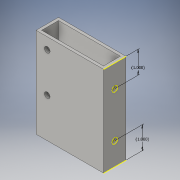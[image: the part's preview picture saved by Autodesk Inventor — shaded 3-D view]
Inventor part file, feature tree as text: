
AUTODESK INVENTOR PART (.ipt)
format: ipt  version: 2016 (Build 200138000, 138)  size: 123,904 bytes
history: native  units: in
note: dims shown in document units (in); Inventor stores cm internally (conversion verified against a paired STEP export)
features: sketch x4, extrude x3
ambient origin geometry x8: Origin, YZ Plane, XZ Plane, XY Plane, X Axis, Y Axis, Z Axis, Center Point
bodies: Solid1 (feature_tree)
feature tree (7):
  extrude  "Extrusion1"  Depth=1.0in
  extrude  "Extrusion2"  Depth=4.0in TaperAngle=0.0deg
  extrude  "Extrusion3"  Depth=1.0in
  sketch  "Sketch4"  dims[d7=1.0in d8=0.125in d9=0.0in d10=0.25in d11=0.5in d12=0.5in d13=0.5in d14=1.75in d15=0.125in d16=0.0in d17=1.0in d18=1.0in]
  sketch  "Sketch1"  dims[d0=3.0in d1=1.0in]
  sketch  "Sketch2"  dims[d2=0.125in d3=4.0in d4=0.0in]
  sketch  "Sketch3"  dims[d5=0.25in d6=1.0in]
